# Revit family: Construction_Roof-Accessories_Alpine-SnowGuards_SnowMax-Standing_Seam_Fence
name_source: partatom
category: Specialty Equipment
units: mm (PartAtom-declared; Revit-internal decimal feet)

## family parameters
Cut with Voids When Loaded = No
Host = Face
OmniClass Number = 23.35.20.31.27.14
OmniClass Title = Snow Guards
Part Type = Normal
Room Calculation Point = No
Round Connector Dimension = Use Diameter
Shared = No

## types (1)
- SnowMax - Standing Seam
    Assembly Code = B3010
    Default Elevation = 48"
    Description = SnowMax Standing Seam bar-style snow guard brackets. Multiple block configurations available for different seam styles.
    Edition number = 1
    Horizontal Spacing = 10"
    Keynote = 07720
    Manufacturer = Alpine SnowGuards
    Model = SnowMax - Standing Seam
    Pad Material = Alpine SnowGuards - Aluminium - Mill Finish
    Product Guid = 787b4320-6630-4dac-a0b9-7ab4bf20129e
    Product Material = Alpine SnowGuards - Aluminium - Mill Finish
    Product data url = https://www.bimobject.com
    T2 = No
    U2 = No
    URL = https://www.alpinesnowguards.com
    UT2 = Yes
    Z2 = No

## geometry (parser evidence)
native form markers: Sweep x6
no freeform markers — native parametric forms only
